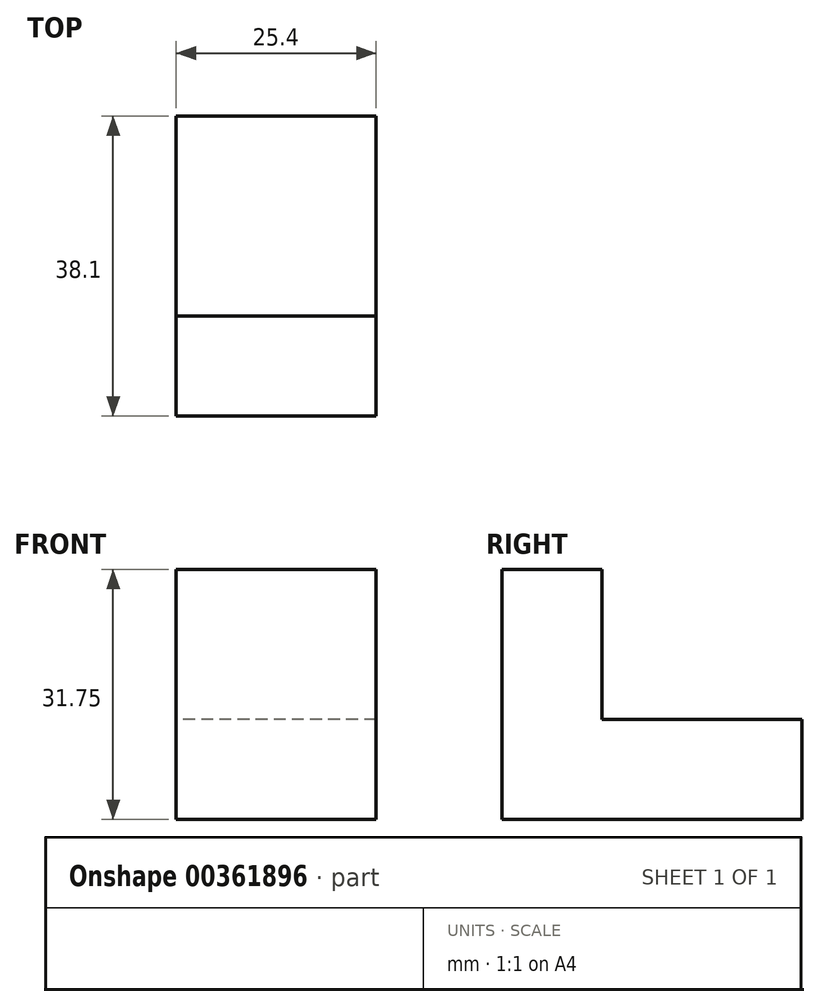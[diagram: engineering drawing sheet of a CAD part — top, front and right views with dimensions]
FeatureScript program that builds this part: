
annotation { "Feature Type Name" : "Feature", "Feature Type Description" : "" }
export const myFeature = defineFeature(function(context is Context, id is Id, definition is map)
    precondition{}
    {
        {
            var Q0;
            Q0=qCreatedBy(makeId("Right.planeOp"),FACE);
            var sketch = newSketch(context, id + "F0", { "sketchPlane" : qUnion([Q0])});
            skLineSegment(sketch, "E0", {"start": v(0, 0) * mm, "end": v(-38.1, 0) * mm});
            skLineSegment(sketch, "E1", {"start": v(-38.1, 0) * mm, "end": v(-38.1, 31.75) * mm});
            skLineSegment(sketch, "E2", {"start": v(-38.1, 31.75) * mm, "end": v(-25.4, 31.75) * mm});
            skLineSegment(sketch, "E3", {"start": v(-25.4, 31.75) * mm, "end": v(-25.4, 12.7) * mm});
            skLineSegment(sketch, "E4", {"start": v(-25.4, 12.7) * mm, "end": v(0, 12.7) * mm});
            skLineSegment(sketch, "E5", {"start": v(0, 12.7) * mm, "end": v(0, 0) * mm});
            skSolve(sketch);
        }
        {
            var Q0;
            Q0 = qSketchRegion(id + "F0", true);
            extrude(context, id + "F1", {"entities" : qUnion([Q0]), "depth" : 25.4 * mm});
        }
        {
            var Q0;
            Q0 = qSketchRegion(id + "F0", true);
            extrude(context, id + "F2", {"entities" : qUnion([Q0]), "operationType" : NewBodyOperationType.ADD, "depth" : 25.4 * mm});
        }
    });
